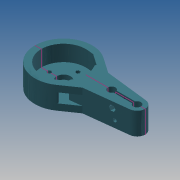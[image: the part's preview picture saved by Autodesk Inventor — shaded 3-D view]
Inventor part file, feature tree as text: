
AUTODESK INVENTOR PART (.ipt)
format: ipt  version: 2013 (Build 170138000, 138)  size: 340,992 bytes
history: native  units: mm
features: sketch x21, extrude x20, projected_geometry x4, mirror x2, chamfer x2, pattern_circular x1, fillet x1
ambient origin geometry x8: Origin, YZ Plane, XZ Plane, XY Plane, X Axis, Y Axis, Z Axis, Center Point
bodies: Solid1 (feature_tree)
feature tree (51):
  extrude  "Extrusion1"  Depth=25.0mm
  extrude  "Extrusion2"  Depth=12.0mm
  extrude  "Extrusion3"  Depth=40.0mm
  extrude  "Extrusion4"  Depth=10.0mm
  pattern_circular  "Circular Pattern1"  Count=4 Angle=360.0deg
  extrude  "Extrusion5"  Depth=4.0mm TaperAngle=0.0deg
  extrude  "Extrusion6"  Depth=7.0mm TaperAngle=0.0deg
  extrude  "Extrusion13"  Depth=6.5mm
  sketch  "Sketch14"  dims[d30=40.0mm d36=6.5mm]
  mirror  "Mirror1"
  extrude  "Extrusion14"  Depth=17.0mm
  extrude  "Extrusion15"  Depth=10.0mm
  extrude  "Extrusion16"  Depth=13.0mm TaperAngle=45.0deg
  extrude  "Extrusion17"  Depth=100.0mm TaperAngle=0.0deg
  extrude  "Extrusion18"  Depth=13.0mm TaperAngle=0.0deg
  extrude  "Extrusion19"  Depth=8.0mm
  fillet  "Fillet2"  Radius=63.662031mm
  extrude  "Extrusion21"  Depth=10000.0mm TaperAngle=0.0deg
  mirror  "Mirror2"
  extrude  "Extrusion22"  Depth=10.725mm
  extrude  "Extrusion8"  Depth=5.5mm
  extrude  "Extrusion9"  Depth=29.0mm TaperAngle=0.0deg
  chamfer  "Chamfer1"  Distance=25.475mm
  extrude  "Extrusion10"  Depth=5.5mm
  extrude  "Extrusion11"  Depth=29.0mm TaperAngle=0.0deg
  chamfer  "Chamfer2"  Distance=8.0mm
  extrude  "Extrusion12"  Depth=10000.0mm TaperAngle=0.0deg
  sketch  "Sketch1"  dims[d0=90.0mm d2=25.0mm]
  sketch  "Sketch2"  dims[d3=115.5mm d4=12.0mm]
  sketch  "Sketch3"  dims[d5=12.062153mm d6=40.0mm]
  sketch  "Sketch4"  dims[d7=35.0mm d8=0.0mm d9=10.0mm]
  sketch  "Sketch5"  dims[d10=25.0mm d11=0.0mm]
  sketch  "Sketch6"  dims[d12=22.5mm]
  sketch  "Sketch8"  dims[d13=3.5mm]
  sketch  "Sketch9"  dims[d14=25.0mm d15=0.0mm]
  sketch  "Sketch10"  dims[d16=5.5mm]
  sketch  "Sketch11"  dims[d17=4.0mm d18=0.0mm d19=40.0mm d20=360.0deg]
  sketch  "Sketch12"  dims[d22=15.0mm d24=4.0mm d25=0.0mm]
  sketch  "Sketch13"  dims[d26=22.0mm d28=7.0mm d29=0.0mm]
  sketch  "Sketch16"  dims[d37=5.5mm d38=17.0mm]
  sketch  "Sketch17"  dims[d39=10.0mm d40=0.0mm d41=10.0mm]
  sketch  "Sketch18"  dims[d43=13.0mm d44=0.0mm d45=13.0mm d46=2.0mm d47=45.0deg]
  sketch  "Sketch19"  dims[d48=8.0mm d49=100.0mm d50=5.0mm d51=0.0mm d52=0.0mm]
  sketch  "Sketch20"  dims[d53=10.0mm d55=13.0mm d56=0.0mm]
  sketch  "Sketch21"  dims[d57=13.0mm d58=2.0mm d59=45.0deg d60=8.0mm]
  sketch  "Sketch23"  dims[d61=10000.0mm d62=5.0mm d63=0.0mm d64=0.0mm d67=63.662031mm]
  projected_geometry  "Projected Loop1"
  sketch  "Sketch24"  dims[d69=6.0mm d70=10000.0mm d71=0.0mm d72=10.725mm d73=5.5mm d74=29.0mm d75=0.0mm d76=25.475mm d77=5.5mm d78=29.0mm d79=0.0mm d80=8.0mm d81=10000.0mm d82=5.0mm d83=0.0mm d84=0.0mm d85=8.0mm d86=10000.0mm d87=5.0mm d88=0.0mm d89=0.0mm d90=5.0mm d92=10000.0mm d93=0.0mm d94=2.0mm d96=10000.0mm d97=0.0mm d100=2.5mm d102=10.0mm d103=10.0mm d104=0.0mm d105=10.0mm d106=0.0mm d107=2.0mm]
  projected_geometry  "Projected Loop2"
  projected_geometry  "Projected Loop3"
  projected_geometry  "Project Cut Edges1"
